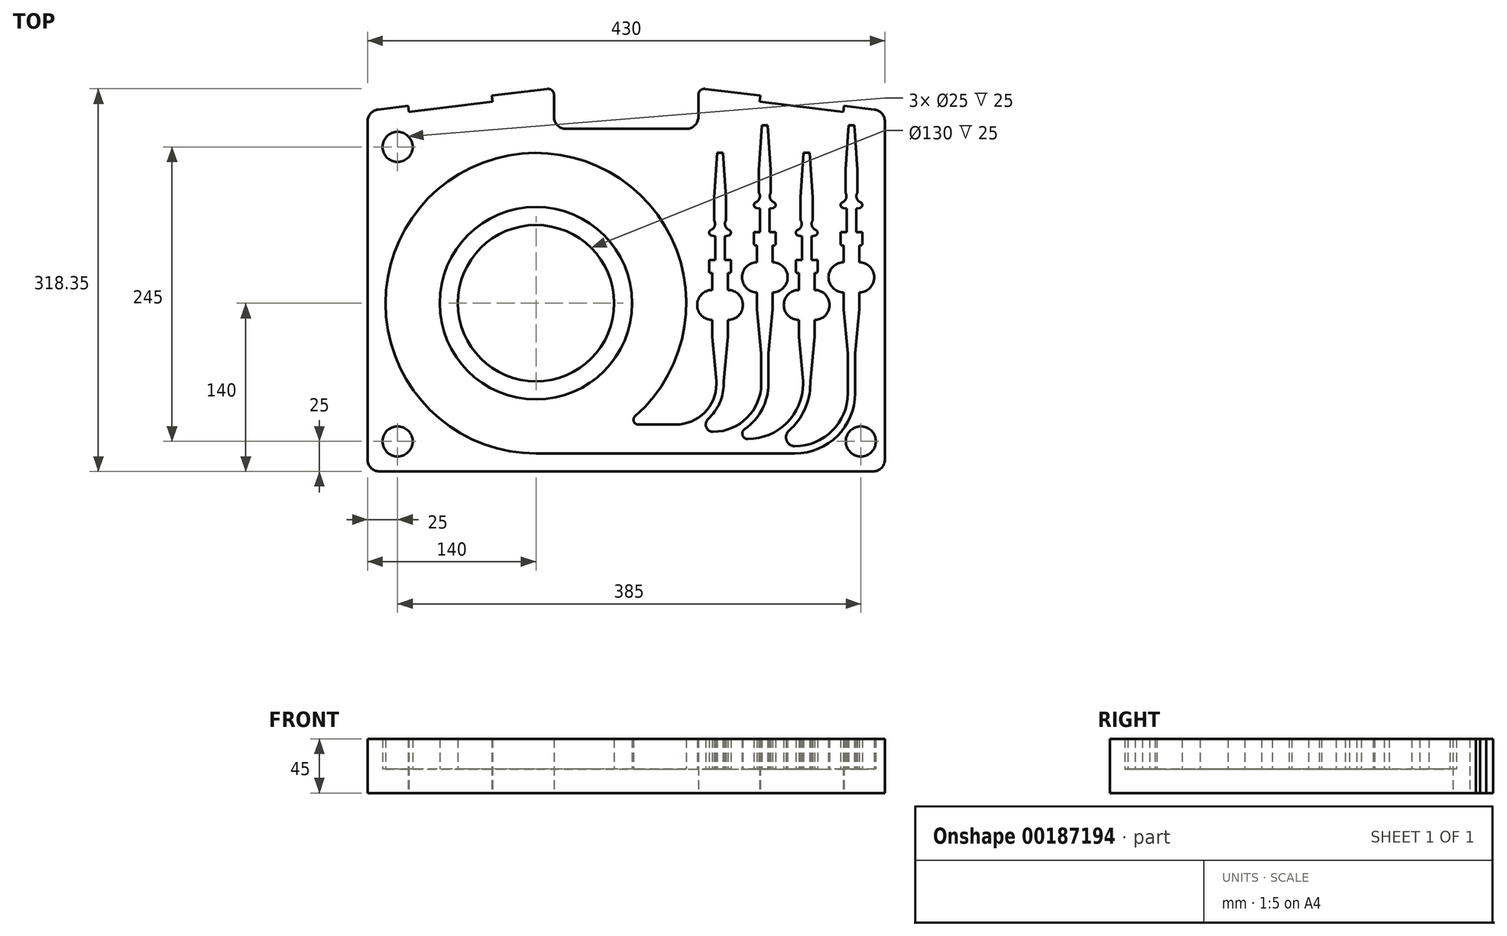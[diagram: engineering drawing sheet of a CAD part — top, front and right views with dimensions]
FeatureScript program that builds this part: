
annotation { "Feature Type Name" : "Feature", "Feature Type Description" : "" }
export const myFeature = defineFeature(function(context is Context, id is Id, definition is map)
    precondition{}
    {
        {
            var Q0;
            Q0=qCreatedBy(makeId("Top.planeOp"),FACE);
            var sketch = newSketch(context, id + "F0", { "sketchPlane" : qUnion([Q0])});
            skLineSegment(sketch, "E0.bottom", {"start": v(10, 0) * mm, "end": v(420, 0) * mm});
            skLineSegment(sketch, "E1.top", {"start": v(165, 285) * mm, "end": v(265, 285) * mm});
            skLineSegment(sketch, "E1.left", {"start": v(155, 313.35) * mm, "end": v(155, 295) * mm});
            skLineSegment(sketch, "E1.right", {"start": v(275, 313.35) * mm, "end": v(275, 295) * mm});
            skLineSegment(sketch, "E2", {"start": v(0, 10) * mm, "end": v(0, 291.15) * mm});
            skLineSegment(sketch, "E3", {"start": v(430, 10) * mm, "end": v(430, 291.15) * mm});
            skLineSegment(sketch, "E4", {"start": v(33.9, 304.16) * mm, "end": v(34.51, 299.2) * mm});
            skLineSegment(sketch, "E5", {"start": v(34.51, 299.2) * mm, "end": v(104, 307.71) * mm});
            skLineSegment(sketch, "E6", {"start": v(104, 307.71) * mm, "end": v(103.39, 312.67) * mm});
            skLineSegment(sketch, "E7", {"start": v(326.61, 312.67) * mm, "end": v(326, 307.71) * mm});
            skLineSegment(sketch, "E8", {"start": v(326, 307.71) * mm, "end": v(395.49, 299.2) * mm});
            skLineSegment(sketch, "E9", {"start": v(395.49, 299.2) * mm, "end": v(396.1, 304.16) * mm});
            skLineSegment(sketch, "E10", {"start": v(396.1, 304.16) * mm, "end": v(421.22, 301.08) * mm});
            skLineSegment(sketch, "E11", {"start": v(326.61, 312.67) * mm, "end": v(280.6, 318.31) * mm});
            skLineSegment(sketch, "E12", {"start": v(103.39, 312.67) * mm, "end": v(149.4, 318.31) * mm});
            skLineSegment(sketch, "E13", {"start": v(8.78, 301.08) * mm, "end": v(33.9, 304.16) * mm});
            skPoint(sketch, "E14.visualSharp", {"position": v(155, 285) * mm});
            skArc(sketch, "E14.filletArc", {"start": v(155, 295) * mm, "mid": v(157.93, 287.93) * mm, "end": v(165, 285) * mm});
            skPoint(sketch, "E15.visualSharp", {"position": v(275, 285) * mm});
            skArc(sketch, "E15.filletArc", {"start": v(265, 285) * mm, "mid": v(272.07, 287.93) * mm, "end": v(275, 295) * mm});
            skPoint(sketch, "E16.visualSharp", {"position": v(430, 300) * mm});
            skArc(sketch, "E16.filletArc", {"start": v(430, 291.15) * mm, "mid": v(427.49, 297.78) * mm, "end": v(421.22, 301.08) * mm});
            skPoint(sketch, "E17.visualSharp", {"position": v(0, 300) * mm});
            skArc(sketch, "E17.filletArc", {"start": v(8.78, 301.08) * mm, "mid": v(2.51, 297.78) * mm, "end": v(0, 291.15) * mm});
            skPoint(sketch, "E18.visualSharp", {"position": v(0, 0) * mm});
            skArc(sketch, "E18.filletArc", {"start": v(0, 10) * mm, "mid": v(2.93, 2.93) * mm, "end": v(10, 0) * mm});
            skPoint(sketch, "E19.visualSharp", {"position": v(430, 0) * mm});
            skArc(sketch, "E19.filletArc", {"start": v(420, 0) * mm, "mid": v(427.07, 2.93) * mm, "end": v(430, 10) * mm});
            skPoint(sketch, "E20.visualSharp", {"position": v(155, 319) * mm});
            skArc(sketch, "E20.filletArc", {"start": v(155, 313.35) * mm, "mid": v(153.31, 317.1) * mm, "end": v(149.4, 318.31) * mm});
            skPoint(sketch, "E21.visualSharp", {"position": v(275, 319) * mm});
            skArc(sketch, "E21.filletArc", {"start": v(280.6, 318.31) * mm, "mid": v(276.69, 317.1) * mm, "end": v(275, 313.35) * mm});
            skLineSegment(sketch, "E22.bottom", {"start": v(286.5, 112) * mm, "end": v(286.5, 126) * mm});
            skLineSegment(sketch, "E22.top", {"start": v(299.5, 112) * mm, "end": v(299.5, 126) * mm});
            skLineSegment(sketch, "E23", {"start": v(293, 75) * mm, "end": v(293, 265) * mm, "construction": true});
            skLineSegment(sketch, "E24", {"start": v(296, 75) * mm, "end": v(299.5, 112) * mm});
            skLineSegment(sketch, "E25", {"start": v(290, 75) * mm, "end": v(286.5, 112) * mm});
            skLineSegment(sketch, "E26.bottom", {"start": v(284, 166.5) * mm, "end": v(284, 176) * mm});
            skLineSegment(sketch, "E26.top", {"start": v(302, 166.5) * mm, "end": v(302, 176) * mm});
            skLineSegment(sketch, "E26.left", {"start": v(285.5, 165) * mm, "end": v(286.5, 165) * mm});
            skLineSegment(sketch, "E26.right", {"start": v(284, 176) * mm, "end": v(289, 176) * mm});
            skPoint(sketch, "E27.visualSharp", {"position": v(284, 165) * mm});
            skArc(sketch, "E27.filletArc", {"start": v(284, 166.5) * mm, "mid": v(284.44, 165.44) * mm, "end": v(285.5, 165) * mm});
            skPoint(sketch, "E28.visualSharp", {"position": v(302, 165) * mm});
            skArc(sketch, "E28.filletArc", {"start": v(300.5, 165) * mm, "mid": v(301.56, 165.44) * mm, "end": v(302, 166.5) * mm});
            skLineSegment(sketch, "E29.trimOffspring", {"start": v(299.5, 165) * mm, "end": v(300.5, 165) * mm});
            skLineSegment(sketch, "E30.bottom", {"start": v(289, 176) * mm, "end": v(289, 195.72) * mm});
            skLineSegment(sketch, "E30.top", {"start": v(297, 176) * mm, "end": v(297, 195.72) * mm});
            skLineSegment(sketch, "E31.trimOffspring", {"start": v(297, 176) * mm, "end": v(302, 176) * mm});
            skLineSegment(sketch, "E32.left", {"start": v(286.08, 196.22) * mm, "end": v(289, 195.72) * mm});
            skLineSegment(sketch, "E33.trimOffspring", {"start": v(297, 195.72) * mm, "end": v(299.92, 196.22) * mm});
            skLineSegment(sketch, "E34.bottom", {"start": v(288, 209) * mm, "end": v(288, 228) * mm});
            skLineSegment(sketch, "E34.top", {"start": v(298, 209) * mm, "end": v(298, 228) * mm});
            skArc(sketch, "E35", {"start": v(285.55, 201) * mm, "mid": v(288.67, 204.42) * mm, "end": v(288, 209) * mm});
            skArc(sketch, "E36", {"start": v(298, 209) * mm, "mid": v(297.33, 204.42) * mm, "end": v(300.45, 201) * mm});
            skArc(sketch, "E37", {"start": v(285.55, 201) * mm, "mid": v(284.02, 198.41) * mm, "end": v(286.08, 196.22) * mm});
            skArc(sketch, "E38", {"start": v(299.92, 196.22) * mm, "mid": v(301.98, 198.41) * mm, "end": v(300.45, 201) * mm});
            skLineSegment(sketch, "E39", {"start": v(298, 228) * mm, "end": v(295.5, 265) * mm});
            skLineSegment(sketch, "E40", {"start": v(295.5, 265) * mm, "end": v(290.5, 265) * mm});
            skLineSegment(sketch, "E41", {"start": v(290.5, 265) * mm, "end": v(288, 228) * mm});
            skArc(sketch, "E42", {"start": v(286.5, 151) * mm, "mid": v(274, 138.5) * mm, "end": v(286.5, 126) * mm});
            skLineSegment(sketch, "E43.trimOffspring", {"start": v(286.5, 151) * mm, "end": v(286.5, 165) * mm});
            skArc(sketch, "E44", {"start": v(299.5, 126) * mm, "mid": v(312, 138.5) * mm, "end": v(299.5, 151) * mm});
            skLineSegment(sketch, "E45.trimOffspring", {"start": v(299.5, 151) * mm, "end": v(299.5, 165) * mm});
            skArc(sketch, "E46", {"start": v(222.4, 46) * mm, "mid": v(95.98, 257) * mm, "end": v(140, 15) * mm});
            skCircle(sketch, "E47", {"center": v(140, 140) * mm, "radius": 80 * mm});
            skCircle(sketch, "E48", {"center": v(140, 140) * mm, "radius": 65 * mm});
            skLineSegment(sketch, "E49", {"start": v(140, 15) * mm, "end": v(355.2, 15) * mm});
            skLineSegment(sketch, "E50", {"start": v(405.2, 65) * mm, "end": v(405.2, 98) * mm});
            skArc(sketch, "E51.filletArc", {"start": v(355.2, 15) * mm, "mid": v(390.56, 29.64) * mm, "end": v(405.2, 65) * mm});
            skLineSegment(sketch, "E52", {"start": v(368, 75) * mm, "end": v(368, 73) * mm});
            skArc(sketch, "E53.filletArc", {"start": v(350.32, 33.94) * mm, "mid": v(363.38, 51.56) * mm, "end": v(368, 73) * mm});
            skLineSegment(sketch, "E54", {"start": v(333.2, 98) * mm, "end": v(333.2, 73) * mm});
            skArc(sketch, "E55.filletArc", {"start": v(313.43, 35.21) * mm, "mid": v(327.96, 51.68) * mm, "end": v(333.2, 73) * mm});
            skLineSegment(sketch, "E56", {"start": v(296, 75) * mm, "end": v(296, 73) * mm});
            skArc(sketch, "E57.filletArc", {"start": v(283.08, 43.56) * mm, "mid": v(292.63, 56.93) * mm, "end": v(296, 73) * mm});
            skLineSegment(sketch, "E58", {"start": v(399.2, 65) * mm, "end": v(399.2, 98) * mm});
            skArc(sketch, "E59.filletArc", {"start": v(355.2, 21) * mm, "mid": v(386.31, 33.89) * mm, "end": v(399.2, 65) * mm});
            skLineSegment(sketch, "E60", {"start": v(362, 73) * mm, "end": v(362, 75) * mm});
            skArc(sketch, "E61.filletArc", {"start": v(316, 27) * mm, "mid": v(348.53, 40.47) * mm, "end": v(362, 73) * mm});
            skLineSegment(sketch, "E62", {"start": v(327.2, 73) * mm, "end": v(327.2, 98) * mm});
            skArc(sketch, "E63.filletArc", {"start": v(287.2, 33) * mm, "mid": v(315.48, 44.72) * mm, "end": v(327.2, 73) * mm});
            skLineSegment(sketch, "E64", {"start": v(225.04, 39) * mm, "end": v(256, 39) * mm});
            skLineSegment(sketch, "E65", {"start": v(290, 73) * mm, "end": v(290, 75) * mm});
            skArc(sketch, "E66", {"start": v(287.2, 33) * mm, "mid": v(281.53, 36.87) * mm, "end": v(283.08, 43.56) * mm});
            skArc(sketch, "E67", {"start": v(316, 27) * mm, "mid": v(311.7, 30.16) * mm, "end": v(313.43, 35.21) * mm});
            skArc(sketch, "E68", {"start": v(355.2, 21) * mm, "mid": v(348.29, 25.78) * mm, "end": v(350.32, 33.94) * mm});
            skArc(sketch, "E69", {"start": v(222.4, 46) * mm, "mid": v(221.3, 41.6) * mm, "end": v(225.04, 39) * mm});
            skArc(sketch, "E70", {"start": v(290, 73) * mm, "mid": v(280.04, 48.96) * mm, "end": v(256, 39) * mm});
            skLineSegment(sketch, "E71.0.1.0", {"start": v(333.2, 98) * mm, "end": v(336.7, 135) * mm});
            skLineSegment(sketch, "E71.0.1.1", {"start": v(336.7, 174) * mm, "end": v(336.7, 188) * mm});
            skPoint(sketch, "E71.0.1.2", {"position": v(321.2, 188) * mm});
            skLineSegment(sketch, "E71.0.1.3", {"start": v(326.2, 199) * mm, "end": v(326.2, 218.72) * mm});
            skLineSegment(sketch, "E71.0.1.4", {"start": v(330.2, 98) * mm, "end": v(330.2, 288) * mm, "construction": true});
            skLineSegment(sketch, "E71.0.1.5", {"start": v(323.7, 174) * mm, "end": v(323.7, 188) * mm});
            skLineSegment(sketch, "E71.0.1.6", {"start": v(325.2, 232) * mm, "end": v(325.2, 251) * mm});
            skLineSegment(sketch, "E71.0.1.7", {"start": v(327.7, 288) * mm, "end": v(325.2, 251) * mm});
            skLineSegment(sketch, "E71.0.1.8", {"start": v(335.2, 232) * mm, "end": v(335.2, 251) * mm});
            skLineSegment(sketch, "E71.0.1.9", {"start": v(327.2, 98) * mm, "end": v(323.7, 135) * mm});
            skLineSegment(sketch, "E71.0.1.10", {"start": v(323.7, 135) * mm, "end": v(323.7, 149) * mm});
            skArc(sketch, "E71.0.1.11", {"start": v(336.7, 149) * mm, "mid": v(349.2, 161.5) * mm, "end": v(336.7, 174) * mm});
            skPoint(sketch, "E71.0.1.12", {"position": v(339.2, 188) * mm});
            skLineSegment(sketch, "E71.0.1.13", {"start": v(334.2, 199) * mm, "end": v(334.2, 218.72) * mm});
            skLineSegment(sketch, "E71.0.1.14", {"start": v(335.2, 251) * mm, "end": v(332.7, 288) * mm});
            skArc(sketch, "E71.0.1.15", {"start": v(323.7, 174) * mm, "mid": v(311.2, 161.5) * mm, "end": v(323.7, 149) * mm});
            skLineSegment(sketch, "E71.0.1.16", {"start": v(336.7, 135) * mm, "end": v(336.7, 149) * mm});
            skArc(sketch, "E71.0.1.17", {"start": v(322.75, 224) * mm, "mid": v(325.87, 227.42) * mm, "end": v(325.2, 232) * mm});
            skLineSegment(sketch, "E71.0.1.18", {"start": v(321.2, 189.5) * mm, "end": v(321.2, 199) * mm});
            skLineSegment(sketch, "E71.0.1.19", {"start": v(339.2, 189.5) * mm, "end": v(339.2, 199) * mm});
            skArc(sketch, "E71.0.1.20", {"start": v(322.75, 224) * mm, "mid": v(321.22, 221.41) * mm, "end": v(323.28, 219.22) * mm});
            skLineSegment(sketch, "E71.0.1.21", {"start": v(334.2, 218.72) * mm, "end": v(337.12, 219.22) * mm});
            skArc(sketch, "E71.0.1.22", {"start": v(337.12, 219.22) * mm, "mid": v(339.18, 221.41) * mm, "end": v(337.65, 224) * mm});
            skArc(sketch, "E71.0.1.23", {"start": v(335.2, 232) * mm, "mid": v(334.53, 227.42) * mm, "end": v(337.65, 224) * mm});
            skLineSegment(sketch, "E71.0.1.24", {"start": v(321.2, 199) * mm, "end": v(326.2, 199) * mm});
            skLineSegment(sketch, "E71.0.1.25", {"start": v(323.28, 219.22) * mm, "end": v(326.2, 218.72) * mm});
            skLineSegment(sketch, "E71.0.1.26", {"start": v(334.2, 199) * mm, "end": v(339.2, 199) * mm});
            skLineSegment(sketch, "E71.0.1.27", {"start": v(336.7, 188) * mm, "end": v(337.7, 188) * mm});
            skArc(sketch, "E71.0.1.28", {"start": v(321.2, 189.5) * mm, "mid": v(321.64, 188.44) * mm, "end": v(322.7, 188) * mm});
            skLineSegment(sketch, "E71.0.1.29", {"start": v(332.7, 288) * mm, "end": v(327.7, 288) * mm});
            skArc(sketch, "E71.0.1.30", {"start": v(337.7, 188) * mm, "mid": v(338.76, 188.44) * mm, "end": v(339.2, 189.5) * mm});
            skLineSegment(sketch, "E71.0.1.31", {"start": v(322.7, 188) * mm, "end": v(323.7, 188) * mm});
            skLineSegment(sketch, "E71.1.0.0", {"start": v(368, 75) * mm, "end": v(371.5, 112) * mm});
            skLineSegment(sketch, "E71.1.0.1", {"start": v(371.5, 151) * mm, "end": v(371.5, 165) * mm});
            skPoint(sketch, "E71.1.0.2", {"position": v(356, 165) * mm});
            skLineSegment(sketch, "E71.1.0.3", {"start": v(361, 176) * mm, "end": v(361, 195.72) * mm});
            skLineSegment(sketch, "E71.1.0.4", {"start": v(365, 75) * mm, "end": v(365, 265) * mm, "construction": true});
            skLineSegment(sketch, "E71.1.0.5", {"start": v(358.5, 151) * mm, "end": v(358.5, 165) * mm});
            skLineSegment(sketch, "E71.1.0.6", {"start": v(360, 209) * mm, "end": v(360, 228) * mm});
            skLineSegment(sketch, "E71.1.0.7", {"start": v(362.5, 265) * mm, "end": v(360, 228) * mm});
            skLineSegment(sketch, "E71.1.0.8", {"start": v(370, 209) * mm, "end": v(370, 228) * mm});
            skLineSegment(sketch, "E71.1.0.9", {"start": v(362, 75) * mm, "end": v(358.5, 112) * mm});
            skLineSegment(sketch, "E71.1.0.10", {"start": v(358.5, 112) * mm, "end": v(358.5, 126) * mm});
            skArc(sketch, "E71.1.0.11", {"start": v(371.5, 126) * mm, "mid": v(384, 138.5) * mm, "end": v(371.5, 151) * mm});
            skPoint(sketch, "E71.1.0.12", {"position": v(374, 165) * mm});
            skLineSegment(sketch, "E71.1.0.13", {"start": v(369, 176) * mm, "end": v(369, 195.72) * mm});
            skLineSegment(sketch, "E71.1.0.14", {"start": v(370, 228) * mm, "end": v(367.5, 265) * mm});
            skArc(sketch, "E71.1.0.15", {"start": v(358.5, 151) * mm, "mid": v(346, 138.5) * mm, "end": v(358.5, 126) * mm});
            skLineSegment(sketch, "E71.1.0.16", {"start": v(371.5, 112) * mm, "end": v(371.5, 126) * mm});
            skArc(sketch, "E71.1.0.17", {"start": v(357.55, 201) * mm, "mid": v(360.67, 204.42) * mm, "end": v(360, 209) * mm});
            skLineSegment(sketch, "E71.1.0.18", {"start": v(356, 166.5) * mm, "end": v(356, 176) * mm});
            skLineSegment(sketch, "E71.1.0.19", {"start": v(374, 166.5) * mm, "end": v(374, 176) * mm});
            skArc(sketch, "E71.1.0.20", {"start": v(357.55, 201) * mm, "mid": v(356.02, 198.41) * mm, "end": v(358.08, 196.22) * mm});
            skLineSegment(sketch, "E71.1.0.21", {"start": v(369, 195.72) * mm, "end": v(371.92, 196.22) * mm});
            skArc(sketch, "E71.1.0.22", {"start": v(371.92, 196.22) * mm, "mid": v(373.98, 198.41) * mm, "end": v(372.45, 201) * mm});
            skArc(sketch, "E71.1.0.23", {"start": v(370, 209) * mm, "mid": v(369.33, 204.42) * mm, "end": v(372.45, 201) * mm});
            skLineSegment(sketch, "E71.1.0.24", {"start": v(356, 176) * mm, "end": v(361, 176) * mm});
            skLineSegment(sketch, "E71.1.0.25", {"start": v(358.08, 196.22) * mm, "end": v(361, 195.72) * mm});
            skLineSegment(sketch, "E71.1.0.26", {"start": v(369, 176) * mm, "end": v(374, 176) * mm});
            skLineSegment(sketch, "E71.1.0.27", {"start": v(371.5, 165) * mm, "end": v(372.5, 165) * mm});
            skArc(sketch, "E71.1.0.28", {"start": v(356, 166.5) * mm, "mid": v(356.44, 165.44) * mm, "end": v(357.5, 165) * mm});
            skLineSegment(sketch, "E71.1.0.29", {"start": v(367.5, 265) * mm, "end": v(362.5, 265) * mm});
            skArc(sketch, "E71.1.0.30", {"start": v(372.5, 165) * mm, "mid": v(373.56, 165.44) * mm, "end": v(374, 166.5) * mm});
            skLineSegment(sketch, "E71.1.0.31", {"start": v(357.5, 165) * mm, "end": v(358.5, 165) * mm});
            skLineSegment(sketch, "E71.1.1.0", {"start": v(405.2, 98) * mm, "end": v(408.7, 135) * mm});
            skLineSegment(sketch, "E71.1.1.1", {"start": v(408.7, 174) * mm, "end": v(408.7, 188) * mm});
            skPoint(sketch, "E71.1.1.2", {"position": v(393.2, 188) * mm});
            skLineSegment(sketch, "E71.1.1.3", {"start": v(398.2, 199) * mm, "end": v(398.2, 218.72) * mm});
            skLineSegment(sketch, "E71.1.1.4", {"start": v(402.2, 98) * mm, "end": v(402.2, 288) * mm, "construction": true});
            skLineSegment(sketch, "E71.1.1.5", {"start": v(395.7, 174) * mm, "end": v(395.7, 188) * mm});
            skLineSegment(sketch, "E71.1.1.6", {"start": v(397.2, 232) * mm, "end": v(397.2, 251) * mm});
            skLineSegment(sketch, "E71.1.1.7", {"start": v(399.7, 288) * mm, "end": v(397.2, 251) * mm});
            skLineSegment(sketch, "E71.1.1.8", {"start": v(407.2, 232) * mm, "end": v(407.2, 251) * mm});
            skLineSegment(sketch, "E71.1.1.9", {"start": v(399.2, 98) * mm, "end": v(395.7, 135) * mm});
            skLineSegment(sketch, "E71.1.1.10", {"start": v(395.7, 135) * mm, "end": v(395.7, 149) * mm});
            skArc(sketch, "E71.1.1.11", {"start": v(408.7, 149) * mm, "mid": v(421.2, 161.5) * mm, "end": v(408.7, 174) * mm});
            skPoint(sketch, "E71.1.1.12", {"position": v(411.2, 188) * mm});
            skLineSegment(sketch, "E71.1.1.13", {"start": v(406.2, 199) * mm, "end": v(406.2, 218.72) * mm});
            skLineSegment(sketch, "E71.1.1.14", {"start": v(407.2, 251) * mm, "end": v(404.7, 288) * mm});
            skArc(sketch, "E71.1.1.15", {"start": v(395.7, 174) * mm, "mid": v(383.2, 161.5) * mm, "end": v(395.7, 149) * mm});
            skLineSegment(sketch, "E71.1.1.16", {"start": v(408.7, 135) * mm, "end": v(408.7, 149) * mm});
            skArc(sketch, "E71.1.1.17", {"start": v(394.75, 224) * mm, "mid": v(397.87, 227.42) * mm, "end": v(397.2, 232) * mm});
            skLineSegment(sketch, "E71.1.1.18", {"start": v(393.2, 189.5) * mm, "end": v(393.2, 199) * mm});
            skLineSegment(sketch, "E71.1.1.19", {"start": v(411.2, 189.5) * mm, "end": v(411.2, 199) * mm});
            skArc(sketch, "E71.1.1.20", {"start": v(394.75, 224) * mm, "mid": v(393.22, 221.41) * mm, "end": v(395.28, 219.22) * mm});
            skLineSegment(sketch, "E71.1.1.21", {"start": v(406.2, 218.72) * mm, "end": v(409.12, 219.22) * mm});
            skArc(sketch, "E71.1.1.22", {"start": v(409.12, 219.22) * mm, "mid": v(411.18, 221.41) * mm, "end": v(409.65, 224) * mm});
            skArc(sketch, "E71.1.1.23", {"start": v(407.2, 232) * mm, "mid": v(406.53, 227.42) * mm, "end": v(409.65, 224) * mm});
            skLineSegment(sketch, "E71.1.1.24", {"start": v(393.2, 199) * mm, "end": v(398.2, 199) * mm});
            skLineSegment(sketch, "E71.1.1.25", {"start": v(395.28, 219.22) * mm, "end": v(398.2, 218.72) * mm});
            skLineSegment(sketch, "E71.1.1.26", {"start": v(406.2, 199) * mm, "end": v(411.2, 199) * mm});
            skLineSegment(sketch, "E71.1.1.27", {"start": v(408.7, 188) * mm, "end": v(409.7, 188) * mm});
            skArc(sketch, "E71.1.1.28", {"start": v(393.2, 189.5) * mm, "mid": v(393.64, 188.44) * mm, "end": v(394.7, 188) * mm});
            skLineSegment(sketch, "E71.1.1.29", {"start": v(404.7, 288) * mm, "end": v(399.7, 288) * mm});
            skArc(sketch, "E71.1.1.30", {"start": v(409.7, 188) * mm, "mid": v(410.76, 188.44) * mm, "end": v(411.2, 189.5) * mm});
            skLineSegment(sketch, "E71.1.1.31", {"start": v(394.7, 188) * mm, "end": v(395.7, 188) * mm});
            skLineSegment(sketch, "E71.direction1", {"start": v(290, 75) * mm, "end": v(362, 75) * mm, "construction": true});
            skLineSegment(sketch, "E71.direction2", {"start": v(290, 75) * mm, "end": v(327.2, 98) * mm, "construction": true});
            skCircle(sketch, "E72", {"center": v(25, 270) * mm, "radius": 12.5 * mm});
            skCircle(sketch, "E73", {"center": v(25, 25) * mm, "radius": 12.5 * mm});
            skCircle(sketch, "E74", {"center": v(410, 25) * mm, "radius": 12.5 * mm});
            skSolve(sketch);
        }
        {
            var Q0;
            Q0 = qSketchRegion(id + "F0", true);
            extrude(context, id + "F1", {"entities" : qUnion([Q0]), "depth" : 25 * mm});
        }
        {
            var Q0;
            Q0=makeQuery(id+"F0.imprint","IMPRINT",FACE,{"disambiguationData":[TD([[makeQuery(id+"F0.imprint","IMPRINT",EDGE,{"derivedFrom":sQuery(id+"F0.wireOp",EDGE,"E47")}),1.0]])]});
            extrude(context, id + "F2", {"entities" : qUnion([Q0]), "depth" : 25 * mm});
        }
        {
            var Q0;
            Q0=makeQuery(id+"F0.imprint","IMPRINT",FACE,{"disambiguationData":[TD([[makeQuery(id+"F0.imprint","IMPRINT",EDGE,{"derivedFrom":sQuery(id+"F0.wireOp",EDGE,"E0.bottom")}),1.0]])]});
            var Q1;
            Q1=makeQuery(id+"F0.imprint","IMPRINT",FACE,{"disambiguationData":[TD([[makeQuery(id+"F0.imprint","IMPRINT",EDGE,{"derivedFrom":sQuery(id+"F0.wireOp",EDGE,"E22.bottom")}),-1.0]])]});
            var Q2;
            Q2=makeQuery(id+"F0.imprint","IMPRINT",FACE,{"disambiguationData":[TD([[makeQuery(id+"F0.imprint","IMPRINT",EDGE,{"derivedFrom":sQuery(id+"F0.wireOp",EDGE,"E47")}),1.0]])]});
            var Q3;
            Q3=makeQuery(id+"F0.imprint","IMPRINT",FACE,{"disambiguationData":[TD([[makeQuery(id+"F0.imprint","IMPRINT",EDGE,{"derivedFrom":sQuery(id+"F0.wireOp",EDGE,"E48")}),1.0]])]});
            var Q4;
            Q4=makeQuery(id+"F0.imprint","IMPRINT",FACE,{"disambiguationData":[TD([[makeQuery(id+"F0.imprint","IMPRINT",EDGE,{"derivedFrom":sQuery(id+"F0.wireOp",EDGE,"E72")}),1.0]])]});
            var Q5;
            Q5=makeQuery(id+"F0.imprint","IMPRINT",FACE,{"disambiguationData":[TD([[makeQuery(id+"F0.imprint","IMPRINT",EDGE,{"derivedFrom":sQuery(id+"F0.wireOp",EDGE,"E73")}),1.0]])]});
            var Q6;
            Q6=makeQuery(id+"F0.imprint","IMPRINT",FACE,{"disambiguationData":[TD([[makeQuery(id+"F0.imprint","IMPRINT",EDGE,{"derivedFrom":sQuery(id+"F0.wireOp",EDGE,"E74")}),1.0]])]});
            extrude(context, id + "F3", {"entities" : qUnion([Q0, Q1, Q2, Q3, Q4, Q5, Q6]), "operationType" : NewBodyOperationType.ADD, "oppositeDirection" : true, "depth" : 20 * mm});
        }
    });
